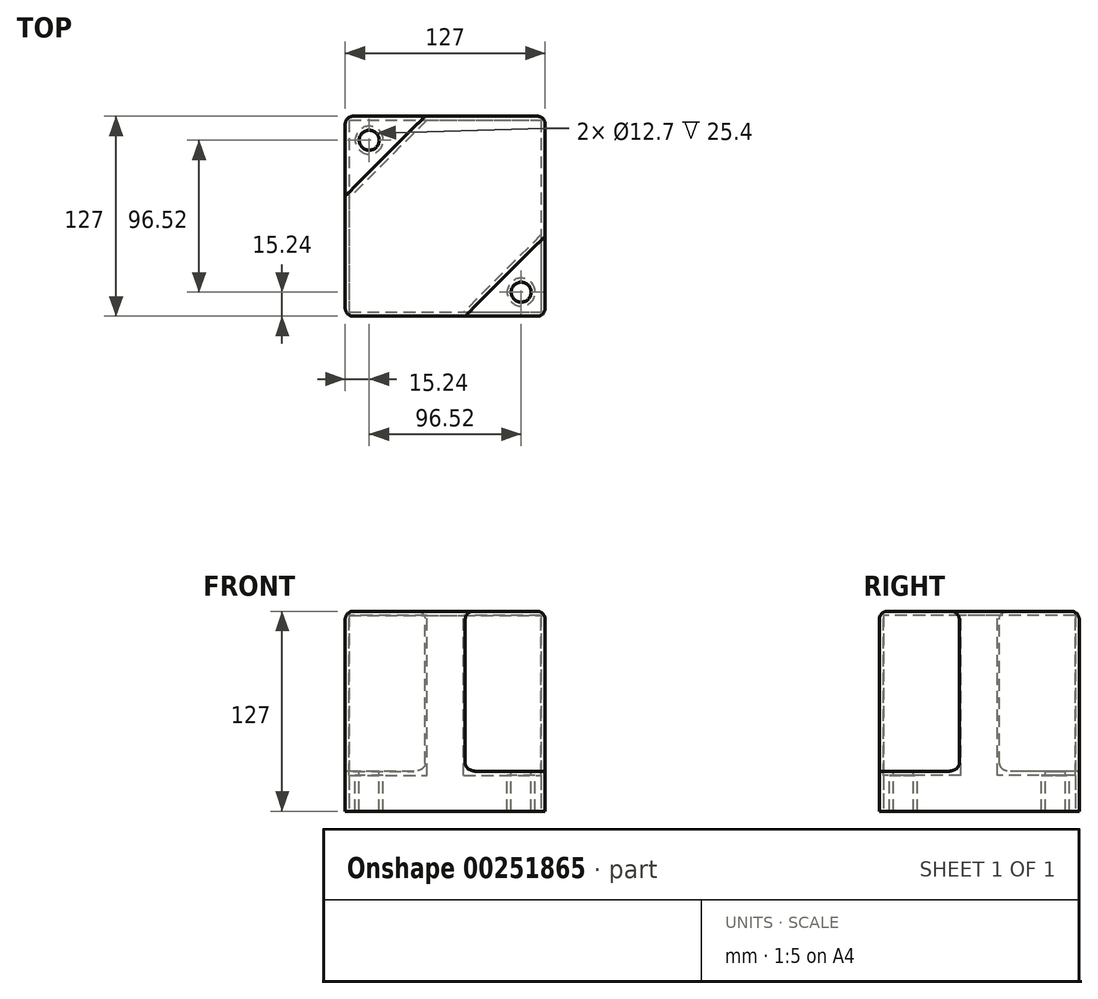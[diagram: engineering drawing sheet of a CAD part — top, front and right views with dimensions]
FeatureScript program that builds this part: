
annotation { "Feature Type Name" : "Feature", "Feature Type Description" : "" }
export const myFeature = defineFeature(function(context is Context, id is Id, definition is map)
    precondition{}
    {
        {
            var Q0;
            Q0=qCreatedBy(makeId("Top.planeOp"),FACE);
            var sketch = newSketch(context, id + "F0", { "sketchPlane" : qUnion([Q0])});
            skLineSegment(sketch, "E0.bottom", {"start": v(-63.5, 63.5) * mm, "end": v(63.5, 63.5) * mm});
            skLineSegment(sketch, "E0.top", {"start": v(-63.5, -63.5) * mm, "end": v(63.5, -63.5) * mm});
            skLineSegment(sketch, "E0.left", {"start": v(-63.5, 63.5) * mm, "end": v(-63.5, -63.5) * mm});
            skLineSegment(sketch, "E0.right", {"start": v(63.5, 63.5) * mm, "end": v(63.5, -63.5) * mm});
            skPoint(sketch, "E0.middle", {"position": v(0, 0) * mm});
            skSolve(sketch);
        }
        {
            var Q0;
            Q0 = qSketchRegion(id + "F0", true);
            extrude(context, id + "F1", {"entities" : qUnion([Q0]), "endBound" : BoundingType.SYMMETRIC, "depth" : 127 * mm});
        }
        {
            var Q0;
            Q0=makeQuery(id+"F1.opExtrude","CAP_FACE",FACE,{"disambiguationData":[OSD([sQuery(id+"F0.wireOp",EDGE,"E0.bottom"),sQuery(id+"F0.wireOp",EDGE,"E0.top"),sQuery(id+"F0.wireOp",EDGE,"E0.left"),sQuery(id+"F0.wireOp",EDGE,"E0.right")])],"isStart":false});
            var sketch = newSketch(context, id + "F2", { "sketchPlane" : qUnion([Q0])});
            skLineSegment(sketch, "E1", {"start": v(-63.5, 63.5) * mm, "end": v(-63.5, 12.7) * mm});
            skLineSegment(sketch, "E2", {"start": v(-63.5, 63.5) * mm, "end": v(-12.7, 63.5) * mm});
            skLineSegment(sketch, "E3", {"start": v(-12.7, 63.5) * mm, "end": v(-63.5, 12.7) * mm});
            skLineSegment(sketch, "E4", {"start": v(63.5, -63.5) * mm, "end": v(63.5, -12.7) * mm});
            skLineSegment(sketch, "E5", {"start": v(63.5, -63.5) * mm, "end": v(12.7, -63.5) * mm});
            skLineSegment(sketch, "E6", {"start": v(63.5, -12.7) * mm, "end": v(12.7, -63.5) * mm});
            skSolve(sketch);
        }
        {
            var Q0;
            Q0=makeQuery(id+"F2.imprint","IMPRINT",FACE,{"disambiguationData":[TD([[makeQuery(id+"F2.imprint","IMPRINT",EDGE,{"derivedFrom":sQuery(id+"F2.wireOp",EDGE,"E1")}),1.0]])]});
            var Q1;
            Q1=makeQuery(id+"F2.imprint","IMPRINT",FACE,{"disambiguationData":[TD([[makeQuery(id+"F2.imprint","IMPRINT",EDGE,{"derivedFrom":sQuery(id+"F2.wireOp",EDGE,"E4")}),-1.0]])]});
            extrude(context, id + "F3", {"entities" : qUnion([Q0, Q1]), "operationType" : NewBodyOperationType.REMOVE, "oppositeDirection" : true, "depth" : 101.6 * mm});
        }
        {
            var Q0;
            Q0=makeQuery(id+"F3.boolean.opBoolean","COPY",FACE,{"derivedFrom":makeQuery(id+"F3.opExtrude","CAP_FACE",FACE,{"disambiguationData":[OSD([sQuery(id+"F2.wireOp",EDGE,"E1"),sQuery(id+"F2.wireOp",EDGE,"E2"),sQuery(id+"F2.wireOp",EDGE,"E3")])],"isStart":false})});
            var sketch = newSketch(context, id + "F4", { "sketchPlane" : qUnion([Q0])});
            skLineSegment(sketch, "E7", {"start": v(-63.5, 63.5) * mm, "end": v(-48.26, 63.5) * mm});
            skLineSegment(sketch, "E8", {"start": v(-48.26, 63.5) * mm, "end": v(-63.5, 63.5) * mm});
            skLineSegment(sketch, "E9", {"start": v(-63.5, 63.5) * mm, "end": v(-63.5, 48.26) * mm});
            skCircle(sketch, "E10", {"center": v(-48.26, 48.26) * mm, "radius": 6.35 * mm});
            skSolve(sketch);
        }
        {
            var Q0;
            Q0=makeQuery(id+"F3.boolean.opBoolean","COPY",FACE,{"derivedFrom":makeQuery(id+"F3.opExtrude","CAP_FACE",FACE,{"disambiguationData":[OSD([sQuery(id+"F2.wireOp",EDGE,"E4"),sQuery(id+"F2.wireOp",EDGE,"E5"),sQuery(id+"F2.wireOp",EDGE,"E6")])],"isStart":false})});
            var sketch = newSketch(context, id + "F5", { "sketchPlane" : qUnion([Q0])});
            skLineSegment(sketch, "E11", {"start": v(63.5, -63.5) * mm, "end": v(48.26, -63.5) * mm});
            skLineSegment(sketch, "E12", {"start": v(63.5, -63.5) * mm, "end": v(63.5, -48.26) * mm});
            skCircle(sketch, "E13", {"center": v(48.26, -48.26) * mm, "radius": 6.35 * mm});
            skSolve(sketch);
        }
        {
            var Q0;
            Q0=makeQuery(id+"F4.imprint","IMPRINT",FACE,{"disambiguationData":[TD([[makeQuery(id+"F4.imprint","IMPRINT",EDGE,{"derivedFrom":sQuery(id+"F4.wireOp",EDGE,"E10")}),1.0]])]});
            var Q1;
            Q1=makeQuery(id+"F5.imprint","IMPRINT",FACE,{"disambiguationData":[TD([[makeQuery(id+"F5.imprint","IMPRINT",EDGE,{"derivedFrom":sQuery(id+"F5.wireOp",EDGE,"E13")}),1.0]])]});
            extrude(context, id + "F6", {"entities" : qUnion([Q0, Q1]), "operationType" : NewBodyOperationType.REMOVE, "oppositeDirection" : true, "depth" : 203.2 * mm});
        }
        {
            var Q0;
            Q0=makeQuery(id+"F1.opExtrude","CAP_FACE",FACE,{"disambiguationData":[OSD([sQuery(id+"F0.wireOp",EDGE,"E0.bottom"),sQuery(id+"F0.wireOp",EDGE,"E0.top"),sQuery(id+"F0.wireOp",EDGE,"E0.left"),sQuery(id+"F0.wireOp",EDGE,"E0.right")])],"isStart":true});
            shell(context, id + "F7", {"entities" : qUnion([Q0]), "thickness" : 2.54 * mm});
        }
        {
            var Q0;
            Q0=makeQuery(id+"F1.opExtrude","SWEPT_EDGE",EDGE,{"disambiguationData":[OSD([sQuery(id+"F0.wireOp",EDGE,"E0.bottom"),sQuery(id+"F0.wireOp",EDGE,"E0.left")])]});
            var Q1;
            Q1=makeQuery(id+"F3.boolean.opBoolean","COPY",EDGE,{"derivedFrom":makeQuery(id+"F3.opExtrude","CAP_EDGE",EDGE,{"disambiguationData":[OSD([sQuery(id+"F2.wireOp",EDGE,"E2")])],"isStart":false})});
            var Q2;
            Q2=makeQuery(id+"F3.boolean.opBoolean","COPY",EDGE,{"derivedFrom":makeQuery(id+"F3.opExtrude","CAP_EDGE",EDGE,{"disambiguationData":[OSD([sQuery(id+"F2.wireOp",EDGE,"E1")])],"isStart":false})});
            var Q3;
            Q3=makeQuery(id+"F1.opExtrude","SWEPT_EDGE",EDGE,{"disambiguationData":[OSD([sQuery(id+"F0.wireOp",EDGE,"E0.top"),sQuery(id+"F0.wireOp",EDGE,"E0.right")])]});
            var Q4;
            Q4=makeQuery(id+"F3.boolean.opBoolean","COPY",EDGE,{"derivedFrom":makeQuery(id+"F3.opExtrude","CAP_EDGE",EDGE,{"disambiguationData":[OSD([sQuery(id+"F2.wireOp",EDGE,"E4")])],"isStart":false})});
            var Q5;
            Q5=makeQuery(id+"F3.boolean.opBoolean","COPY",EDGE,{"derivedFrom":makeQuery(id+"F3.opExtrude","SWEPT_EDGE",EDGE,{"disambiguationData":[OSD([sQuery(id+"F0.wireOp",EDGE,"E0.right"),sQuery(id+"F2.wireOp",EDGE,"E4"),sQuery(id+"F2.wireOp",EDGE,"E6")])]})});
            var Q6;
            Q6=makeQuery(id+"F3.boolean.opBoolean","COPY",EDGE,{"derivedFrom":makeQuery(id+"F3.opExtrude","SWEPT_EDGE",EDGE,{"disambiguationData":[OSD([sQuery(id+"F0.wireOp",EDGE,"E0.top"),sQuery(id+"F2.wireOp",EDGE,"E5"),sQuery(id+"F2.wireOp",EDGE,"E6")])]})});
            var Q7;
            Q7=makeQuery(id+"F3.boolean.opBoolean","COPY",EDGE,{"derivedFrom":makeQuery(id+"F3.opExtrude","CAP_EDGE",EDGE,{"disambiguationData":[OSD([sQuery(id+"F2.wireOp",EDGE,"E5")])],"isStart":false})});
            var Q8;
            Q8=makeQuery(id+"F3.boolean.opBoolean","COPY",EDGE,{"derivedFrom":makeQuery(id+"F3.opExtrude","CAP_EDGE",EDGE,{"disambiguationData":[OSD([sQuery(id+"F2.wireOp",EDGE,"E6")])],"isStart":false})});
            var Q9;
            Q9=makeQuery(id+"F3.boolean.opBoolean","COPY",EDGE,{"derivedFrom":makeQuery(id+"F3.opExtrude","CAP_EDGE",EDGE,{"disambiguationData":[OSD([sQuery(id+"F2.wireOp",EDGE,"E6")])],"isStart":true})});
            var Q10;
            Q10=makeQuery(id+"F1.opExtrude","CAP_EDGE",EDGE,{"disambiguationData":[OSD([sQuery(id+"F0.wireOp",EDGE,"E0.top")])],"isStart":false});
            var Q11;
            Q11=makeQuery(id+"F1.opExtrude","CAP_EDGE",EDGE,{"disambiguationData":[OSD([sQuery(id+"F0.wireOp",EDGE,"E0.right")])],"isStart":false});
            var Q12;
            Q12=makeQuery(id+"F1.opExtrude","SWEPT_EDGE",EDGE,{"disambiguationData":[OSD([sQuery(id+"F0.wireOp",EDGE,"E0.bottom"),sQuery(id+"F0.wireOp",EDGE,"E0.right")])]});
            var Q13;
            Q13=makeQuery(id+"F1.opExtrude","SWEPT_EDGE",EDGE,{"disambiguationData":[OSD([sQuery(id+"F0.wireOp",EDGE,"E0.top"),sQuery(id+"F0.wireOp",EDGE,"E0.left")])]});
            var Q14;
            Q14=makeQuery(id+"F3.boolean.opBoolean","COPY",EDGE,{"derivedFrom":makeQuery(id+"F3.opExtrude","SWEPT_EDGE",EDGE,{"disambiguationData":[OSD([sQuery(id+"F0.wireOp",EDGE,"E0.left"),sQuery(id+"F2.wireOp",EDGE,"E1"),sQuery(id+"F2.wireOp",EDGE,"E3")])]})});
            var Q15;
            Q15=makeQuery(id+"F1.opExtrude","CAP_EDGE",EDGE,{"disambiguationData":[OSD([sQuery(id+"F0.wireOp",EDGE,"E0.left")])],"isStart":false});
            var Q16;
            Q16=makeQuery(id+"F3.boolean.opBoolean","COPY",EDGE,{"derivedFrom":makeQuery(id+"F3.opExtrude","CAP_EDGE",EDGE,{"disambiguationData":[OSD([sQuery(id+"F2.wireOp",EDGE,"E3")])],"isStart":true})});
            var Q17;
            Q17=makeQuery(id+"F3.boolean.opBoolean","COPY",EDGE,{"derivedFrom":makeQuery(id+"F3.opExtrude","CAP_EDGE",EDGE,{"disambiguationData":[OSD([sQuery(id+"F2.wireOp",EDGE,"E3")])],"isStart":false})});
            var Q18;
            Q18=makeQuery(id+"F1.opExtrude","CAP_EDGE",EDGE,{"disambiguationData":[OSD([sQuery(id+"F0.wireOp",EDGE,"E0.bottom")])],"isStart":false});
            fillet(context, id + "F8", {"entities" : qUnion([Q0, Q1, Q2, Q3, Q4, Q5, Q6, Q7, Q8, Q9, Q10, Q11, Q12, Q13, Q14, Q15, Q16, Q17, Q18]), "radius" : 5.08 * mm, "tangentPropagation" : true, "allowEdgeOverflow" : false});
        }
    });
